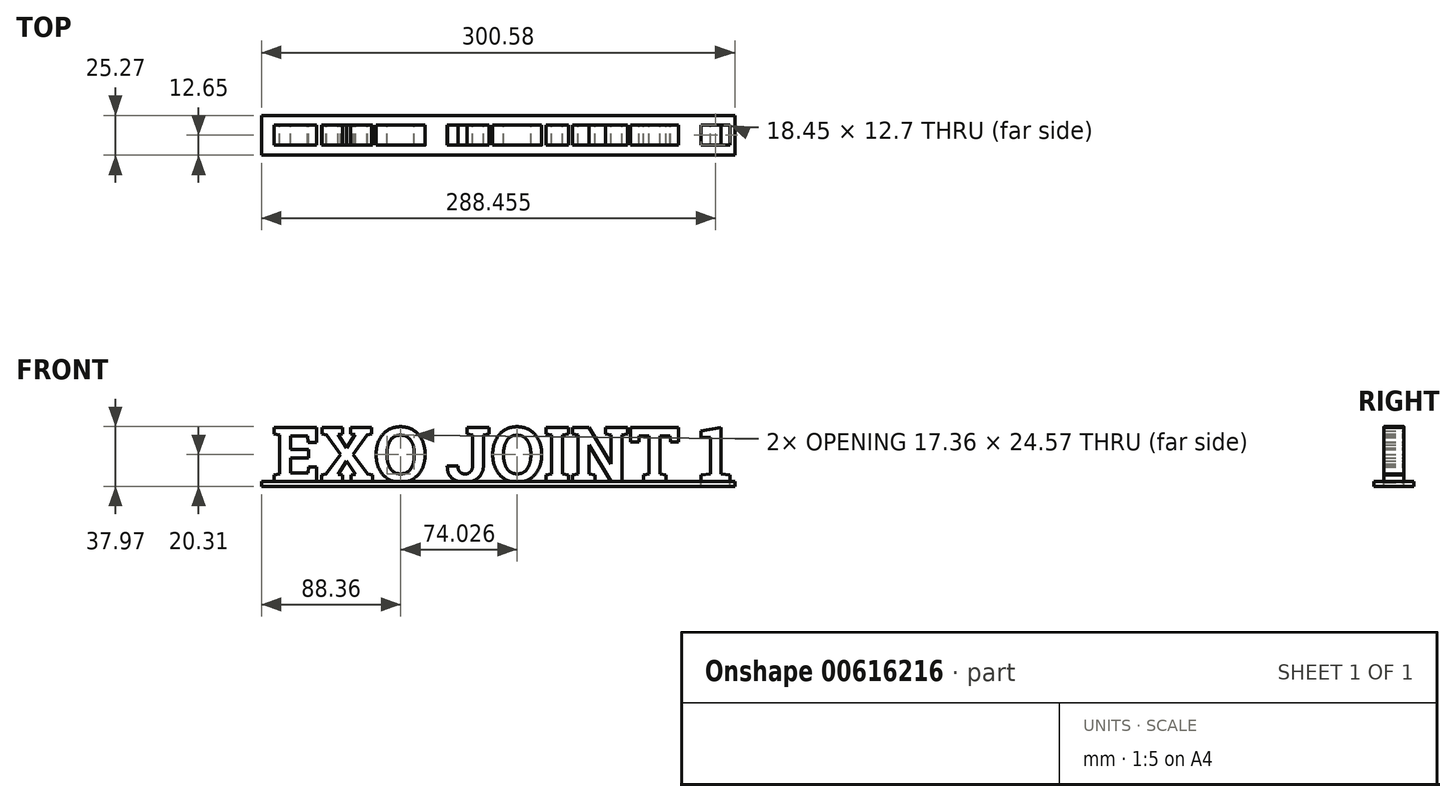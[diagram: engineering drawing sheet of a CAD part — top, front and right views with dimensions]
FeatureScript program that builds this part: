
annotation { "Feature Type Name" : "Feature", "Feature Type Description" : "" }
export const myFeature = defineFeature(function(context is Context, id is Id, definition is map)
    precondition{}
    {
        {
            var Q0;
            Q0=qCreatedBy(makeId("Front.planeOp"),FACE);
            var sketch = newSketch(context, id + "F0", { "sketchPlane" : qUnion([Q0])});
            skText(sketch, "E0", { "text": "EXO JOINT 1", "fontName": "RobotoSlab-Bold.ttf"});
            const initialGuessF0  = {"E0": [-0.14832, -0.01562, 1, 0, 0.03474]};
            skSetInitialGuess(sketch, initialGuessF0);
            skSolve(sketch);
        }
        {
            var Q0;
            Q0=qSketchRegion(id+"F0",true);
            extrude(context, id + "F1", {"entities" : qUnion([Q0]), "depth" : 12.7 * mm});
        }
        {
            var Q0;
            Q0=makeQuery(id+"F1.opExtrude","SWEPT_FACE",FACE,{"disambiguationData":[OSD([sQuery(id+"F0.wireOp",EDGE,"E0.sketch_text.stroke-167")])]});
            var sketch = newSketch(context, id + "F2", { "sketchPlane" : qUnion([Q0])});
            skLineSegment(sketch, "E1.bottom", {"start": v(-154.84, 19) * mm, "end": v(145.74, 19) * mm});
            skLineSegment(sketch, "E1.top", {"start": v(-154.84, -6.27) * mm, "end": v(145.74, -6.27) * mm});
            skLineSegment(sketch, "E1.left", {"start": v(-154.84, 19) * mm, "end": v(-154.84, -6.27) * mm});
            skLineSegment(sketch, "E1.right", {"start": v(145.74, 19) * mm, "end": v(145.74, -6.27) * mm});
            skSolve(sketch);
        }
        {
            var Q0;
            Q0=makeQuery(id+"F2.imprint","IMPRINT",FACE,{"disambiguationData":[TD([[makeQuery(id+"F2.imprint","IMPRINT",EDGE,{"derivedFrom":sQuery(id+"F2.wireOp",EDGE,"E1.bottom")}),-1.0]])]});
            extrude(context, id + "F3", {"entities" : qUnion([Q0]), "depth" : 3.17 * mm});
        }
    });
